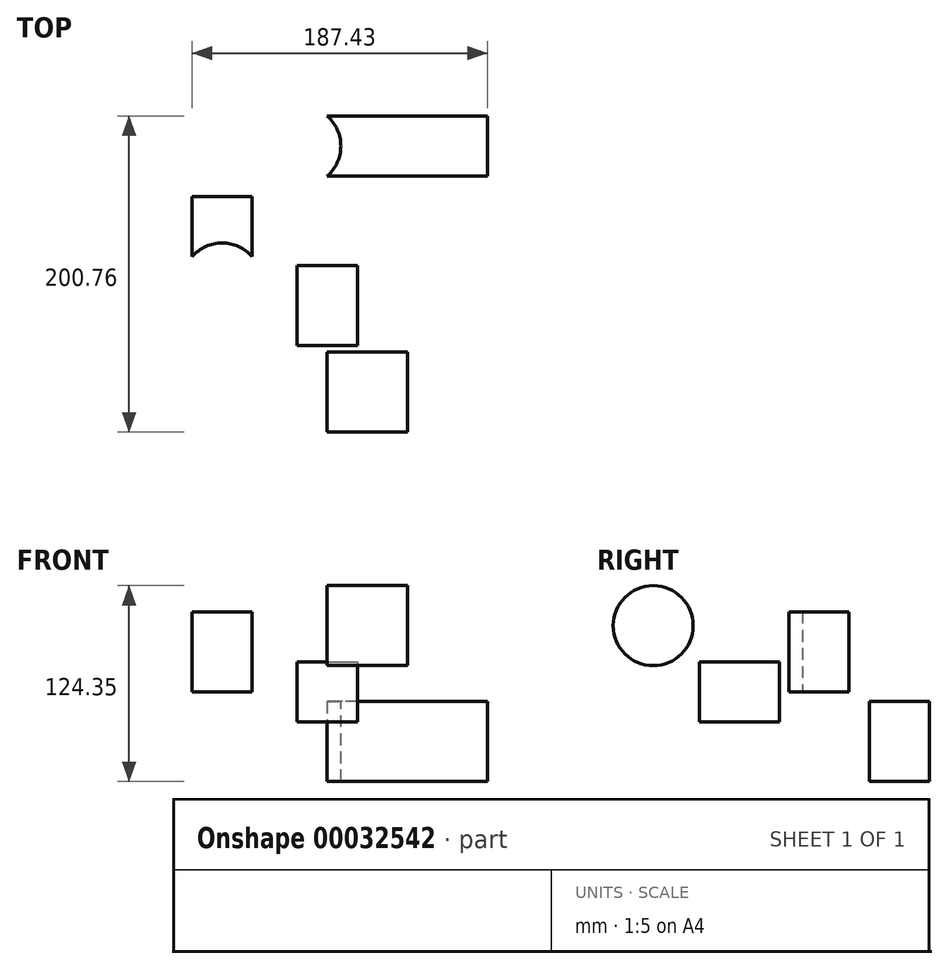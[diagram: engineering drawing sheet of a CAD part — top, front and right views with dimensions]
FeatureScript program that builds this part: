
annotation { "Feature Type Name" : "Feature", "Feature Type Description" : "" }
export const myFeature = defineFeature(function(context is Context, id is Id, definition is map)
    precondition{}
    {
        {
            var Q0;
            Q0=qCreatedBy(makeId("Front.planeOp"),FACE);
            var sketch = newSketch(context, id + "F0", { "sketchPlane" : qUnion([Q0])});
            skLineSegment(sketch, "E0.rect.bottom", {"start": v(-19.05, 19.05) * mm, "end": v(19.05, 19.05) * mm});
            skLineSegment(sketch, "E0.rect.top", {"start": v(-19.05, -19.05) * mm, "end": v(19.05, -19.05) * mm});
            skLineSegment(sketch, "E0.rect.left", {"start": v(-19.05, 19.05) * mm, "end": v(-19.05, -19.05) * mm});
            skLineSegment(sketch, "E0.rect.right", {"start": v(19.05, 19.05) * mm, "end": v(19.05, -19.05) * mm});
            skPoint(sketch, "E0.rect.middle", {"position": v(0, 0) * mm});
            skSolve(sketch);
        }
        {
            var Q0;
            Q0 = qSketchRegion(id + "F0", true);
            extrude(context, id + "F1", {"entities" : qUnion([Q0]), "depth" : 50.8 * mm});
        }
        {
            var Q0;
            Q0=qCreatedBy(makeId("Top.planeOp"),FACE);
            var sketch = newSketch(context, id + "F2", { "sketchPlane" : qUnion([Q0])});
            skLineSegment(sketch, "E1.rect.bottom", {"start": v(-85.83, 43.93) * mm, "end": v(-47.73, 43.93) * mm});
            skLineSegment(sketch, "E1.rect.top", {"start": v(-85.83, 5.83) * mm, "end": v(-47.73, 5.83) * mm});
            skLineSegment(sketch, "E1.rect.left", {"start": v(-85.83, 43.93) * mm, "end": v(-85.83, 5.83) * mm});
            skLineSegment(sketch, "E1.rect.right", {"start": v(-47.73, 43.93) * mm, "end": v(-47.73, 5.83) * mm});
            skPoint(sketch, "E1.rect.middle", {"position": v(-66.78, 24.88) * mm});
            skSolve(sketch);
        }
        {
            var Q0;
            Q0 = qSketchRegion(id + "F2", true);
            extrude(context, id + "F3", {"entities" : qUnion([Q0]), "depth" : 50.8 * mm});
        }
        {
            var Q0;
            Q0=qCreatedBy(makeId("Right.planeOp"),FACE);
            var sketch = newSketch(context, id + "F4", { "sketchPlane" : qUnion([Q0])});
            skCircle(sketch, "E2", {"center": v(-80.3, 42.05) * mm, "radius": 25.4 * mm});
            skSolve(sketch);
        }
        {
            var Q0;
            Q0 = qSketchRegion(id + "F4", true);
            extrude(context, id + "F5", {"entities" : qUnion([Q0]), "depth" : 50.8 * mm});
        }
        {
            var Q0;
            Q0=makeQuery(id+"F3.opExtrude","CAP_FACE",FACE,{"disambiguationData":[OSD([sQuery(id+"F2.wireOp",EDGE,"E1.rect.bottom"),sQuery(id+"F2.wireOp",EDGE,"E1.rect.top"),sQuery(id+"F2.wireOp",EDGE,"E1.rect.left"),sQuery(id+"F2.wireOp",EDGE,"E1.rect.right")])],"isStart":true});
            var sketch = newSketch(context, id + "F6", { "sketchPlane" : qUnion([Q0])});
            skArc(sketch, "E3", {"start": v(-85.83, -5.83) * mm, "mid": v(-66.78, -14.43) * mm, "end": v(-47.73, -5.83) * mm});
            skSolve(sketch);
        }
        {
            var Q0;
            Q0 = qSketchRegion(id + "F6", true);
            var Q1;
            Q1=makeQuery(id+"F6.imprint","IMPRINT",FACE,{"disambiguationData":[TD([[makeQuery(id+"F6.imprint","IMPRINT",EDGE,{"derivedFrom":sQuery(id+"F6.wireOp",EDGE,"E3")}),1.0]])]});
            extrude(context, id + "F7", {"entities" : qUnion([Q0, Q1]), "operationType" : NewBodyOperationType.REMOVE, "endBound" : BoundingType.THROUGH_ALL, "oppositeDirection" : true, "depth" : 25.4 * mm});
        }
        {
            var Q0;
            Q0=qCreatedBy(makeId("Right.planeOp"),FACE);
            var sketch = newSketch(context, id + "F8", { "sketchPlane" : qUnion([Q0])});
            skLineSegment(sketch, "E4.rect.bottom", {"start": v(56.96, -6.1) * mm, "end": v(95.06, -6.1) * mm});
            skLineSegment(sketch, "E4.rect.top", {"start": v(56.96, -56.9) * mm, "end": v(95.06, -56.9) * mm});
            skLineSegment(sketch, "E4.rect.left", {"start": v(56.96, -6.1) * mm, "end": v(56.96, -56.9) * mm});
            skLineSegment(sketch, "E4.rect.right", {"start": v(95.06, -6.1) * mm, "end": v(95.06, -56.9) * mm});
            skPoint(sketch, "E4.rect.middle", {"position": v(76.01, -31.5) * mm});
            skSolve(sketch);
        }
        {
            var Q0;
            Q0 = qSketchRegion(id + "F8", true);
            extrude(context, id + "F9", {"entities" : qUnion([Q0]), "depth" : 101.6 * mm});
        }
        {
            var Q0;
            Q0=makeQuery(id+"F9.opExtrude","SWEPT_FACE",FACE,{"disambiguationData":[OSD([sQuery(id+"F8.wireOp",EDGE,"E4.rect.bottom")])]});
            var sketch = newSketch(context, id + "F10", { "sketchPlane" : qUnion([Q0])});
            skArc(sketch, "E5", {"start": v(0, 56.96) * mm, "mid": v(8.6, 76.01) * mm, "end": v(0, 95.06) * mm});
            skSolve(sketch);
        }
        {
            var Q0;
            Q0 = qSketchRegion(id + "F10", true);
            var Q1;
            Q1=makeQuery(id+"F10.imprint","IMPRINT",FACE,{"disambiguationData":[TD([[makeQuery(id+"F10.imprint","IMPRINT",EDGE,{"derivedFrom":sQuery(id+"F10.wireOp",EDGE,"E5")}),1.0]])]});
            extrude(context, id + "F11", {"entities" : qUnion([Q0, Q1]), "operationType" : NewBodyOperationType.REMOVE, "endBound" : BoundingType.THROUGH_ALL, "oppositeDirection" : true, "depth" : 25.4 * mm});
        }
    });
